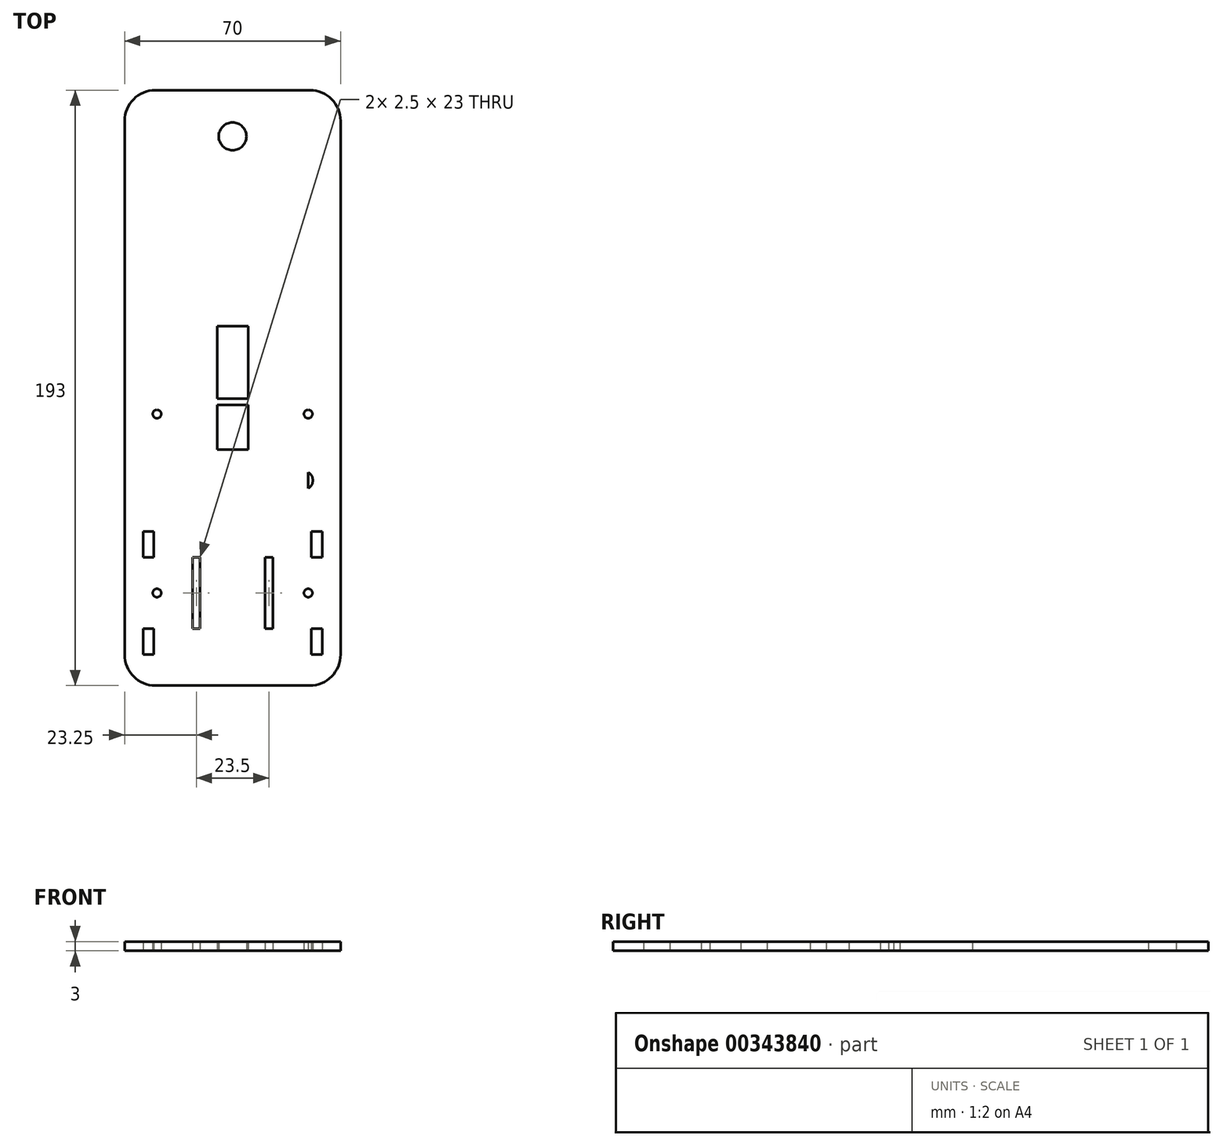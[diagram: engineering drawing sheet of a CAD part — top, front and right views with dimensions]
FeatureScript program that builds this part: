
annotation { "Feature Type Name" : "Feature", "Feature Type Description" : "" }
export const myFeature = defineFeature(function(context is Context, id is Id, definition is map)
    precondition{}
    {
        {
            var Q0;
            Q0=qCreatedBy(makeId("Top.planeOp"),FACE);
            var sketch = newSketch(context, id + "F0", { "sketchPlane" : qUnion([Q0])});
            skLineSegment(sketch, "E0.bottom", {"start": v(-25, 96.5) * mm, "end": v(25, 96.5) * mm});
            skLineSegment(sketch, "E0.top", {"start": v(-25, -96.5) * mm, "end": v(25, -96.5) * mm});
            skLineSegment(sketch, "E0.left", {"start": v(-35, 86.5) * mm, "end": v(-35, -86.5) * mm});
            skLineSegment(sketch, "E0.right", {"start": v(35, 86.5) * mm, "end": v(35, -86.5) * mm});
            skPoint(sketch, "E0.middle", {"position": v(0, 0) * mm});
            skLineSegment(sketch, "E1.bottom", {"start": v(-29, -78) * mm, "end": v(-25.5, -78) * mm});
            skLineSegment(sketch, "E1.top", {"start": v(-29, -86.5) * mm, "end": v(-25.5, -86.5) * mm});
            skLineSegment(sketch, "E1.left", {"start": v(-29, -78) * mm, "end": v(-29, -86.5) * mm});
            skLineSegment(sketch, "E1.right", {"start": v(-25.5, -78) * mm, "end": v(-25.5, -86.5) * mm});
            skLineSegment(sketch, "E2.bottom", {"start": v(-29, -55) * mm, "end": v(-25.5, -55) * mm});
            skLineSegment(sketch, "E2.top", {"start": v(-29, -46.5) * mm, "end": v(-25.5, -46.5) * mm});
            skLineSegment(sketch, "E2.left", {"start": v(-29, -55) * mm, "end": v(-29, -46.5) * mm});
            skLineSegment(sketch, "E2.right", {"start": v(-25.5, -55) * mm, "end": v(-25.5, -46.5) * mm});
            skLineSegment(sketch, "E3.MirrorCS", {"start": v(29, -55) * mm, "end": v(25.5, -55) * mm});
            skLineSegment(sketch, "E4.MirrorCS", {"start": v(29, -78) * mm, "end": v(25.5, -78) * mm});
            skLineSegment(sketch, "E5.MirrorCS", {"start": v(29, -86.5) * mm, "end": v(25.5, -86.5) * mm});
            skLineSegment(sketch, "E6.MirrorCS", {"start": v(29, -46.5) * mm, "end": v(25.5, -46.5) * mm});
            skLineSegment(sketch, "E7.MirrorCS", {"start": v(25.5, -55) * mm, "end": v(25.5, -46.5) * mm});
            skLineSegment(sketch, "E8.MirrorCS", {"start": v(29, -78) * mm, "end": v(29, -86.5) * mm});
            skLineSegment(sketch, "E9.MirrorCS", {"start": v(25.5, -78) * mm, "end": v(25.5, -86.5) * mm});
            skLineSegment(sketch, "E10.MirrorCS", {"start": v(29, -55) * mm, "end": v(29, -46.5) * mm});
            skCircle(sketch, "E11", {"center": v(0, 81.5) * mm, "radius": 4.5 * mm});
            skPoint(sketch, "E12.visualSharp", {"position": v(35, 96.5) * mm});
            skArc(sketch, "E12.filletArc", {"start": v(35, 86.5) * mm, "mid": v(32.07, 93.57) * mm, "end": v(25, 96.5) * mm});
            skPoint(sketch, "E13.visualSharp", {"position": v(-35, 96.5) * mm});
            skArc(sketch, "E13.filletArc", {"start": v(-25, 96.5) * mm, "mid": v(-32.07, 93.57) * mm, "end": v(-35, 86.5) * mm});
            skPoint(sketch, "E14.visualSharp", {"position": v(35, -96.5) * mm});
            skArc(sketch, "E14.filletArc", {"start": v(25, -96.5) * mm, "mid": v(32.07, -93.57) * mm, "end": v(35, -86.5) * mm});
            skPoint(sketch, "E15.visualSharp", {"position": v(-35, -96.5) * mm});
            skArc(sketch, "E15.filletArc", {"start": v(-35, -86.5) * mm, "mid": v(-32.07, -93.57) * mm, "end": v(-25, -96.5) * mm});
            skLineSegment(sketch, "E16.bottom", {"start": v(-5, 20) * mm, "end": v(5, 20) * mm});
            skLineSegment(sketch, "E16.top", {"start": v(-5, -20) * mm, "end": v(5, -20) * mm});
            skLineSegment(sketch, "E16.left", {"start": v(-5, 20) * mm, "end": v(-5, -20) * mm});
            skLineSegment(sketch, "E16.right", {"start": v(5, 20) * mm, "end": v(5, -20) * mm});
            skLineSegment(sketch, "E17.bottom", {"start": v(-13, -55) * mm, "end": v(-10.5, -55) * mm});
            skLineSegment(sketch, "E17.top", {"start": v(-13, -78) * mm, "end": v(-10.5, -78) * mm});
            skLineSegment(sketch, "E17.left", {"start": v(-13, -55) * mm, "end": v(-13, -78) * mm});
            skLineSegment(sketch, "E17.right", {"start": v(-10.5, -55) * mm, "end": v(-10.5, -78) * mm});
            skLineSegment(sketch, "E18.MirrorCS", {"start": v(13, -55) * mm, "end": v(10.5, -55) * mm});
            skLineSegment(sketch, "E19.MirrorCS", {"start": v(13, -78) * mm, "end": v(10.5, -78) * mm});
            skLineSegment(sketch, "E20.MirrorCS", {"start": v(10.5, -55) * mm, "end": v(10.5, -78) * mm});
            skLineSegment(sketch, "E21.MirrorCS", {"start": v(13, -55) * mm, "end": v(13, -78) * mm});
            skCircle(sketch, "E22", {"center": v(24.5, -8.5) * mm, "radius": 1.37 * mm});
            skCircle(sketch, "E23", {"center": v(24.5, -66.5) * mm, "radius": 1.38 * mm});
            skCircle(sketch, "E24", {"center": v(-24.5, -66.5) * mm, "radius": 1.38 * mm});
            skCircle(sketch, "E25", {"center": v(-24.5, -8.5) * mm, "radius": 1.38 * mm});
            skLineSegment(sketch, "E26", {"start": v(24.5, -8.5) * mm, "end": v(24.5, -66.5) * mm});
            skLineSegment(sketch, "E27", {"start": v(24.5, -66.5) * mm, "end": v(-24.5, -66.5) * mm});
            skPoint(sketch, "E28", {"position": v(0, -37.5) * mm});
            skPoint(sketch, "E28.positionSnap0", {"position": v(0, -66.5) * mm});
            skPoint(sketch, "E28.positionSnap1", {"position": v(24.5, -37.5) * mm});
            skLineSegment(sketch, "E29.bottom", {"start": v(-13, -55) * mm, "end": v(-18.5, -55) * mm});
            skLineSegment(sketch, "E29.top", {"start": v(-13, -78) * mm, "end": v(-18.5, -78) * mm});
            skLineSegment(sketch, "E29.right", {"start": v(-18.5, -55) * mm, "end": v(-18.5, -78) * mm});
            skLineSegment(sketch, "E30.bottom", {"start": v(-10.5, -78) * mm, "end": v(-25.5, -78) * mm});
            skLineSegment(sketch, "E30.top", {"start": v(-10.5, -86.5) * mm, "end": v(-25.5, -86.5) * mm});
            skLineSegment(sketch, "E30.left", {"start": v(-10.5, -78) * mm, "end": v(-10.5, -86.5) * mm});
            skLineSegment(sketch, "E31.MirrorCS", {"start": v(13, -55) * mm, "end": v(18.5, -55) * mm});
            skLineSegment(sketch, "E32.MirrorCS", {"start": v(18.5, -55) * mm, "end": v(18.5, -78) * mm});
            skLineSegment(sketch, "E33.MirrorCS", {"start": v(10.5, -78) * mm, "end": v(25.5, -78) * mm});
            skLineSegment(sketch, "E34.MirrorCS", {"start": v(10.5, -86.5) * mm, "end": v(25.5, -86.5) * mm});
            skLineSegment(sketch, "E35.MirrorCS", {"start": v(10.5, -78) * mm, "end": v(10.5, -86.5) * mm});
            skLineSegment(sketch, "E36.bottom", {"start": v(-13, -78) * mm, "end": v(-29, -78) * mm});
            skLineSegment(sketch, "E36.top", {"start": v(-13, -55) * mm, "end": v(-29, -55) * mm});
            skLineSegment(sketch, "E36.left", {"start": v(-13, -78) * mm, "end": v(-13, -55) * mm});
            skLineSegment(sketch, "E36.right", {"start": v(-29, -78) * mm, "end": v(-29, -55) * mm});
            skLineSegment(sketch, "E37.MirrorCS", {"start": v(29, -78) * mm, "end": v(29, -55) * mm});
            skLineSegment(sketch, "E38.MirrorCS", {"start": v(13, -55) * mm, "end": v(29, -55) * mm});
            skCircle(sketch, "E39", {"center": v(0, -30) * mm, "radius": 20 * mm});
            skCircle(sketch, "E40.0", {"center": v(0, -30) * mm, "radius": 22 * mm});
            skCircle(sketch, "E41", {"center": v(-23, -30) * mm, "radius": 1 * mm});
            skCircle(sketch, "E42.0", {"center": v(-23, -30) * mm, "radius": 3 * mm});
            skCircle(sketch, "E43.MirrorC", {"center": v(23, -30) * mm, "radius": 1 * mm});
            skCircle(sketch, "E44.MirrorC", {"center": v(23, -30) * mm, "radius": 3 * mm});
            skLineSegment(sketch, "E45", {"start": v(-10.5, -55) * mm, "end": v(10.5, -55) * mm, "construction": true});
            skLineSegment(sketch, "E46.bottom", {"start": v(30, -3.5) * mm, "end": v(-30, -3.5) * mm});
            skLineSegment(sketch, "E46.top", {"start": v(30, 51.5) * mm, "end": v(-30, 51.5) * mm});
            skLineSegment(sketch, "E46.left", {"start": v(30, -3.5) * mm, "end": v(30, 51.5) * mm});
            skLineSegment(sketch, "E46.right", {"start": v(-30, -3.5) * mm, "end": v(-30, 51.5) * mm});
            skPoint(sketch, "E46.middle", {"position": v(0, 24) * mm});
            skLineSegment(sketch, "E47.0", {"start": v(20, 6.5) * mm, "end": v(20, 41.5) * mm});
            skLineSegment(sketch, "E47.1", {"start": v(20, 6.5) * mm, "end": v(-20, 6.5) * mm});
            skLineSegment(sketch, "E47.2", {"start": v(-20, 6.5) * mm, "end": v(-20, 41.5) * mm});
            skLineSegment(sketch, "E47.3", {"start": v(20, 41.5) * mm, "end": v(-20, 41.5) * mm});
            skLineSegment(sketch, "E48.0", {"start": v(32, 53.5) * mm, "end": v(-30, 53.5) * mm});
            skLineSegment(sketch, "E48.1", {"start": v(32, -5.5) * mm, "end": v(32, 53.5) * mm});
            skLineSegment(sketch, "E48.2", {"start": v(32, -5.5) * mm, "end": v(-30, -5.5) * mm});
            skLineSegment(sketch, "E49", {"start": v(-30, 51.5) * mm, "end": v(-30, 53.5) * mm});
            skLineSegment(sketch, "E50", {"start": v(-30, -5.5) * mm, "end": v(-30, -3.5) * mm});
            skLineSegment(sketch, "E51", {"start": v(-20, 41.5) * mm, "end": v(-30, 41.5) * mm});
            skLineSegment(sketch, "E52", {"start": v(20, 41.5) * mm, "end": v(32, 41.5) * mm});
            skLineSegment(sketch, "E53", {"start": v(32, 41.5) * mm, "end": v(20, 41.5) * mm});
            skLineSegment(sketch, "E54", {"start": v(20, 53.5) * mm, "end": v(20, 41.5) * mm});
            skLineSegment(sketch, "E55", {"start": v(20, 6.5) * mm, "end": v(32, 6.5) * mm});
            skLineSegment(sketch, "E56", {"start": v(20, 6.5) * mm, "end": v(20, -5.5) * mm});
            skLineSegment(sketch, "E57", {"start": v(-20, 6.5) * mm, "end": v(-20, -5.5) * mm});
            skLineSegment(sketch, "E58", {"start": v(-20, 41.5) * mm, "end": v(-20, 53.5) * mm});
            skLineSegment(sketch, "E59", {"start": v(-20, 6.5) * mm, "end": v(-30, 6.5) * mm});
            skCircle(sketch, "E60", {"center": v(-17, -8.5) * mm, "radius": 1 * mm});
            skCircle(sketch, "E61.0", {"center": v(-17, -8.5) * mm, "radius": 3 * mm});
            skCircle(sketch, "E62", {"center": v(-27, 56.5) * mm, "radius": 1 * mm});
            skCircle(sketch, "E63.0", {"center": v(-27, 56.5) * mm, "radius": 3 * mm});
            skLineSegment(sketch, "E64", {"start": v(-30, 53.5) * mm, "end": v(-30, 56.5) * mm});
            skLineSegment(sketch, "E65", {"start": v(-24, 56.5) * mm, "end": v(-24, 53.5) * mm});
            skLineSegment(sketch, "E66", {"start": v(-14, -8.5) * mm, "end": v(-14, -5.5) * mm});
            skLineSegment(sketch, "E67", {"start": v(-20, -8.5) * mm, "end": v(-20, -5.5) * mm});
            skLineSegment(sketch, "E68.bottom", {"start": v(-30, 53.5) * mm, "end": v(-32, 53.5) * mm});
            skLineSegment(sketch, "E68.top", {"start": v(-30, -5.5) * mm, "end": v(-32, -5.5) * mm});
            skLineSegment(sketch, "E68.left", {"start": v(-30, 53.5) * mm, "end": v(-30, -5.5) * mm});
            skLineSegment(sketch, "E68.right", {"start": v(-32, 53.5) * mm, "end": v(-32, -5.5) * mm});
            skLineSegment(sketch, "E69", {"start": v(-30, 41.5) * mm, "end": v(-32, 41.5) * mm});
            skLineSegment(sketch, "E70", {"start": v(-30, 6.5) * mm, "end": v(-32, 6.5) * mm});
            skSolve(sketch);
        }
        {
            var Q0;
            Q0=makeQuery(id+"F0.imprint","IMPRINT",FACE,{"disambiguationData":[TD([[makeQuery(id+"F0.imprint","IMPRINT",EDGE,{"derivedFrom":sQuery(id+"F0.wireOp",EDGE,"E0.bottom")}),-1.0]])]});
            var Q1;
            {var subQ0=sQuery(id+"F0.wireOp",EDGE,"0ZoFnGFM-cKHT-HDos-aa4S-ERoNxdyYTCCv.left");Q1=makeQuery(id+"F0.imprint","IMPRINT",FACE,{"disambiguationData":[TD([[makeQuery(id+"F0.imprint","IMPRINT",EDGE,{"derivedFrom":subQ0}),1.0]])]});}
            var Q2;
            {var subQ0=sQuery(id+"F0.wireOp",EDGE,"0ZoFnGFM-cKHT-HDos-aa4S-ERoNxdyYTCCv.left");Q2=makeQuery(id+"F0.imprint","IMPRINT",FACE,{"disambiguationData":[TD([[makeQuery(id+"F0.imprint","IMPRINT",EDGE,{"derivedFrom":subQ0}),-1.0]])]});}
            var Q3;
            {var subQ0=sQuery(id+"F0.wireOp",EDGE,"E29.right");var subQ1=sQuery(id+"F0.wireOp",EDGE,"E27");var subQ2=makeQuery(id+"F0.imprint","INTERSECT",VERTEX,{"derivedFrom":[subQ1,subQ0]});Q3=makeQuery(id+"F0.imprint","IMPRINT",FACE,{"disambiguationData":[TD([[makeQuery(id+"F0.imprint","IMPRINT",EDGE,{"disambiguationData":[TD([[subQ2,1.0]])],"derivedFrom":subQ1}),1.0]])]});}
            var Q4;
            {var subQ5=sQuery(id+"F0.wireOp",EDGE,"E29.bottom");Q4=makeQuery(id+"F0.imprint","IMPRINT",FACE,{"disambiguationData":[TD([[makeQuery(id+"F0.imprint","IMPRINT",EDGE,{"derivedFrom":subQ5}),1.0]])]});}
            var Q5;
            Q5=makeQuery(id+"F0.imprint","IMPRINT",FACE,{"disambiguationData":[TD([[makeQuery(id+"F0.imprint","IMPRINT",EDGE,{"derivedFrom":sQuery(id+"F0.wireOp",EDGE,"E30.top")}),-1.0]])]});
            var Q6;
            {var subQ1=sQuery(id+"F0.wireOp",EDGE,"E9.MirrorCS");Q6=makeQuery(id+"F0.imprint","IMPRINT",FACE,{"disambiguationData":[TD([[makeQuery(id+"F0.imprint","IMPRINT",EDGE,{"derivedFrom":subQ1}),-1.0]])]});}
            var Q7;
            {var subQ0=sQuery(id+"F0.wireOp",EDGE,"E33.MirrorCS");var subQ1=sQuery(id+"F0.wireOp",EDGE,"E21.MirrorCS");var subQ2=makeQuery(id+"F0.imprint","INTERSECT",VERTEX,{"derivedFrom":[subQ1,subQ0]});Q7=makeQuery(id+"F0.imprint","IMPRINT",FACE,{"disambiguationData":[TD([[makeQuery(id+"F0.imprint","IMPRINT",EDGE,{"disambiguationData":[TD([[subQ2,1.0]])],"derivedFrom":subQ1}),1.0]])]});}
            var Q8;
            {var subQ0=sQuery(id+"F0.wireOp",EDGE,"E31.MirrorCS");Q8=makeQuery(id+"F0.imprint","IMPRINT",FACE,{"disambiguationData":[TD([[makeQuery(id+"F0.imprint","IMPRINT",EDGE,{"derivedFrom":subQ0}),-1.0]])]});}
            var Q9;
            Q9=makeQuery(id+"F0.imprint","IMPRINT",FACE,{"disambiguationData":[TD([[makeQuery(id+"F0.imprint","IMPRINT",EDGE,{"derivedFrom":sQuery(id+"F0.wireOp",EDGE,"E24")}),-1.0]])]});
            var Q10;
            {var subQ0=sQuery(id+"F0.wireOp",EDGE,"E29.right");var subQ1=sQuery(id+"F0.wireOp",EDGE,"E27");var subQ2=makeQuery(id+"F0.imprint","INTERSECT",VERTEX,{"derivedFrom":[subQ1,subQ0]});Q10=makeQuery(id+"F0.imprint","IMPRINT",FACE,{"disambiguationData":[TD([[makeQuery(id+"F0.imprint","IMPRINT",EDGE,{"disambiguationData":[TD([[subQ2,1.0]])],"derivedFrom":subQ1}),-1.0]])]});}
            var Q11;
            {var subQ5=sQuery(id+"F0.wireOp",EDGE,"E23");var subQ7=sQuery(id+"F0.wireOp",EDGE,"E26");var subQ9=makeQuery(id+"F0.imprint","INTERSECT",VERTEX,{"derivedFrom":[subQ5,subQ7]});Q11=makeQuery(id+"F0.imprint","IMPRINT",FACE,{"disambiguationData":[TD([[makeQuery(id+"F0.imprint","IMPRINT",EDGE,{"disambiguationData":[TD([[subQ9,-1.0]])],"derivedFrom":subQ5}),-1.0]])]});}
            var Q12;
            {var subQ1=sQuery(id+"F0.wireOp",EDGE,"E21.MirrorCS");var subQ3=sQuery(id+"F0.wireOp",EDGE,"E27");var subQ4=makeQuery(id+"F0.imprint","INTERSECT",VERTEX,{"derivedFrom":[subQ1,subQ3]});Q12=makeQuery(id+"F0.imprint","IMPRINT",FACE,{"disambiguationData":[TD([[makeQuery(id+"F0.imprint","IMPRINT",EDGE,{"disambiguationData":[TD([[subQ4,1.0]])],"derivedFrom":subQ3}),-1.0]])]});}
            var Q13;
            {var subQ11=sQuery(id+"F0.wireOp",EDGE,"E4.MirrorCS");Q13=makeQuery(id+"F0.imprint","IMPRINT",FACE,{"disambiguationData":[TD([[makeQuery(id+"F0.imprint","IMPRINT",EDGE,{"derivedFrom":subQ11}),-1.0]])]});}
            var Q14;
            {var subQ4=sQuery(id+"F0.wireOp",EDGE,"E16.top");Q14=makeQuery(id+"F0.imprint","IMPRINT",FACE,{"disambiguationData":[TD([[makeQuery(id+"F0.imprint","IMPRINT",EDGE,{"derivedFrom":subQ4}),-1.0]])]});}
            var Q15;
            {var subQ0=sQuery(id+"F0.wireOp",EDGE,"E40.0");var subQ1=sQuery(id+"F0.wireOp",EDGE,"E16.left");var subQ2=makeQuery(id+"F0.imprint","INTERSECT",VERTEX,{"derivedFrom":[subQ1,subQ0]});Q15=makeQuery(id+"F0.imprint","IMPRINT",FACE,{"disambiguationData":[TD([[makeQuery(id+"F0.imprint","IMPRINT",EDGE,{"disambiguationData":[TD([[subQ2,-1.0]])],"derivedFrom":subQ1}),-1.0]])]});}
            var Q16;
            {var subQ0=sQuery(id+"F0.wireOp",EDGE,"E40.0");var subQ1=makeQuery(id+"F0.imprint","INTERSECT",VERTEX,{"derivedFrom":[subQ0,sQuery(id+"F0.wireOp",EDGE,"E41")]});Q16=makeQuery(id+"F0.imprint","IMPRINT",FACE,{"disambiguationData":[TD([[makeQuery(id+"F0.imprint","IMPRINT",EDGE,{"disambiguationData":[TD([[subQ1,1.0]])],"derivedFrom":subQ0}),1.0]])]});}
            var Q17;
            {var subQ0=sQuery(id+"F0.wireOp",EDGE,"E44.MirrorC");var subQ1=sQuery(id+"F0.wireOp",EDGE,"E39");var subQ2=makeQuery(id+"F0.imprint","INTERSECT",VERTEX,{"derivedFrom":[subQ1,subQ0]});Q17=makeQuery(id+"F0.imprint","IMPRINT",FACE,{"disambiguationData":[TD([[makeQuery(id+"F0.imprint","IMPRINT",EDGE,{"disambiguationData":[TD([[subQ2,1.0]])],"derivedFrom":subQ1}),-1.0]])]});}
            var Q18;
            {var subQ0=sQuery(id+"F0.wireOp",EDGE,"E41");Q18=makeQuery(id+"F0.imprint","IMPRINT",FACE,{"disambiguationData":[TD([[makeQuery(id+"F0.imprint","IMPRINT",EDGE,{"derivedFrom":subQ0}),-1.0]])]});}
            var Q19;
            Q19=makeQuery(id+"F0.imprint","IMPRINT",FACE,{"disambiguationData":[TD([[makeQuery(id+"F0.imprint","IMPRINT",EDGE,{"derivedFrom":sQuery(id+"F0.wireOp",EDGE,"E41")}),1.0]])]});
            var Q20;
            {var subQ0=sQuery(id+"F0.wireOp",EDGE,"E40.0");var subQ1=makeQuery(id+"F0.imprint","INTERSECT",VERTEX,{"derivedFrom":[subQ0,sQuery(id+"F0.wireOp",EDGE,"E43.MirrorC")]});Q20=makeQuery(id+"F0.imprint","IMPRINT",FACE,{"disambiguationData":[TD([[makeQuery(id+"F0.imprint","IMPRINT",EDGE,{"disambiguationData":[TD([[subQ1,-1.0]])],"derivedFrom":subQ0}),1.0]])]});}
            var Q21;
            {var subQ0=sQuery(id+"F0.wireOp",EDGE,"E40.0");var subQ1=sQuery(id+"F0.wireOp",EDGE,"E16.right");var subQ2=makeQuery(id+"F0.imprint","INTERSECT",VERTEX,{"derivedFrom":[subQ1,subQ0]});Q21=makeQuery(id+"F0.imprint","IMPRINT",FACE,{"disambiguationData":[TD([[makeQuery(id+"F0.imprint","IMPRINT",EDGE,{"disambiguationData":[TD([[subQ2,-1.0]])],"derivedFrom":subQ1}),1.0]])]});}
            var Q22;
            {var subQ0=sQuery(id+"F0.wireOp",EDGE,"E43.MirrorC");Q22=makeQuery(id+"F0.imprint","IMPRINT",FACE,{"disambiguationData":[TD([[makeQuery(id+"F0.imprint","IMPRINT",EDGE,{"derivedFrom":subQ0}),1.0]])]});}
            var Q23;
            {var subQ0=sQuery(id+"F0.wireOp",EDGE,"E44.MirrorC");var subQ1=sQuery(id+"F0.wireOp",EDGE,"E26");var subQ2=makeQuery(id+"F0.imprint","INTERSECT",VERTEX,{"disambiguationData":[OD(0.0)],"derivedFrom":[subQ1,subQ0]});Q23=makeQuery(id+"F0.imprint","IMPRINT",FACE,{"disambiguationData":[TD([[makeQuery(id+"F0.imprint","IMPRINT",EDGE,{"disambiguationData":[TD([[subQ2,-1.0]])],"derivedFrom":subQ1}),1.0]])]});}
            var Q24;
            Q24=makeQuery(id+"F0.imprint","IMPRINT",FACE,{"disambiguationData":[TD([[makeQuery(id+"F0.imprint","IMPRINT",EDGE,{"derivedFrom":sQuery(id+"F0.wireOp",EDGE,"E43.MirrorC")}),-1.0]])]});
            var Q25;
            {var subQ2=sQuery(id+"F0.wireOp",EDGE,"E16.bottom");Q25=makeQuery(id+"F0.imprint","IMPRINT",FACE,{"disambiguationData":[TD([[makeQuery(id+"F0.imprint","IMPRINT",EDGE,{"derivedFrom":subQ2}),1.0]])]});}
            var Q26;
            Q26=makeQuery(id+"F0.imprint","IMPRINT",FACE,{"disambiguationData":[TD([[makeQuery(id+"F0.imprint","IMPRINT",EDGE,{"derivedFrom":sQuery(id+"F0.wireOp",EDGE,"E46.top")}),1.0]])]});
            var Q27;
            Q27=makeQuery(id+"F0.imprint","IMPRINT",FACE,{"disambiguationData":[TD([[makeQuery(id+"F0.imprint","IMPRINT",EDGE,{"derivedFrom":sQuery(id+"F0.wireOp",EDGE,"E46.top")}),-1.0]])]});
            var Q28;
            {var subQ5=sQuery(id+"F0.wireOp",EDGE,"E50");Q28=makeQuery(id+"F0.imprint","IMPRINT",FACE,{"disambiguationData":[TD([[makeQuery(id+"F0.imprint","IMPRINT",EDGE,{"derivedFrom":subQ5}),-1.0]])]});}
            var Q29;
            Q29=makeQuery(id+"F0.imprint","IMPRINT",FACE,{"disambiguationData":[TD([[makeQuery(id+"F0.imprint","IMPRINT",EDGE,{"derivedFrom":sQuery(id+"F0.wireOp",EDGE,"E47.2")}),1.0]])]});
            var Q30;
            {var subQ5=sQuery(id+"F0.wireOp",EDGE,"E59");Q30=makeQuery(id+"F0.imprint","IMPRINT",FACE,{"disambiguationData":[TD([[makeQuery(id+"F0.imprint","IMPRINT",EDGE,{"derivedFrom":subQ5}),1.0]])]});}
            var Q31;
            {var subQ0=sQuery(id+"F0.wireOp",EDGE,"E47.1");var subQ1=sQuery(id+"F0.wireOp",EDGE,"E16.left");var subQ2=makeQuery(id+"F0.imprint","INTERSECT",VERTEX,{"derivedFrom":[subQ1,subQ0]});Q31=makeQuery(id+"F0.imprint","IMPRINT",FACE,{"disambiguationData":[TD([[makeQuery(id+"F0.imprint","IMPRINT",EDGE,{"disambiguationData":[TD([[subQ2,-1.0]])],"derivedFrom":subQ1}),-1.0]])]});}
            var Q32;
            {var subQ0=sQuery(id+"F0.wireOp",EDGE,"E46.bottom");var subQ1=sQuery(id+"F0.wireOp",EDGE,"E16.left");var subQ2=makeQuery(id+"F0.imprint","INTERSECT",VERTEX,{"derivedFrom":[subQ1,subQ0]});Q32=makeQuery(id+"F0.imprint","IMPRINT",FACE,{"disambiguationData":[TD([[makeQuery(id+"F0.imprint","IMPRINT",EDGE,{"disambiguationData":[TD([[subQ2,-1.0]])],"derivedFrom":subQ1}),-1.0]])]});}
            var Q33;
            {var subQ0=sQuery(id+"F0.wireOp",EDGE,"E47.1");var subQ1=sQuery(id+"F0.wireOp",EDGE,"E16.right");var subQ2=makeQuery(id+"F0.imprint","INTERSECT",VERTEX,{"derivedFrom":[subQ1,subQ0]});Q33=makeQuery(id+"F0.imprint","IMPRINT",FACE,{"disambiguationData":[TD([[makeQuery(id+"F0.imprint","IMPRINT",EDGE,{"disambiguationData":[TD([[subQ2,-1.0]])],"derivedFrom":subQ1}),1.0]])]});}
            var Q34;
            {var subQ0=sQuery(id+"F0.wireOp",EDGE,"E46.bottom");var subQ1=sQuery(id+"F0.wireOp",EDGE,"E16.right");var subQ2=makeQuery(id+"F0.imprint","INTERSECT",VERTEX,{"derivedFrom":[subQ1,subQ0]});Q34=makeQuery(id+"F0.imprint","IMPRINT",FACE,{"disambiguationData":[TD([[makeQuery(id+"F0.imprint","IMPRINT",EDGE,{"disambiguationData":[TD([[subQ2,-1.0]])],"derivedFrom":subQ1}),1.0]])]});}
            var Q35;
            {var subQ0=sQuery(id+"F0.wireOp",EDGE,"E46.left");var subQ1=sQuery(id+"F0.wireOp",EDGE,"E46.bottom");var subQ2=makeQuery(id+"F0.imprint","INTERSECT",VERTEX,{"derivedFrom":[subQ1,subQ0]});Q35=makeQuery(id+"F0.imprint","IMPRINT",FACE,{"disambiguationData":[TD([[makeQuery(id+"F0.imprint","IMPRINT",EDGE,{"disambiguationData":[TD([[subQ2,-1.0]])],"derivedFrom":subQ1}),-1.0]])]});}
            var Q36;
            {var subQ0=sQuery(id+"F0.wireOp",EDGE,"E55");var subQ1=sQuery(id+"F0.wireOp",EDGE,"E46.left");var subQ2=makeQuery(id+"F0.imprint","INTERSECT",VERTEX,{"derivedFrom":[subQ1,subQ0]});Q36=makeQuery(id+"F0.imprint","IMPRINT",FACE,{"disambiguationData":[TD([[makeQuery(id+"F0.imprint","IMPRINT",EDGE,{"disambiguationData":[TD([[subQ2,-1.0]])],"derivedFrom":subQ1}),-1.0]])]});}
            var Q37;
            {var subQ7=sQuery(id+"F0.wireOp",EDGE,"E46.left");var subQ8=sQuery(id+"F0.wireOp",EDGE,"E46.bottom");var subQ9=makeQuery(id+"F0.imprint","INTERSECT",VERTEX,{"derivedFrom":[subQ8,subQ7]});Q37=makeQuery(id+"F0.imprint","IMPRINT",FACE,{"disambiguationData":[TD([[makeQuery(id+"F0.imprint","IMPRINT",EDGE,{"disambiguationData":[TD([[subQ9,-1.0]])],"derivedFrom":subQ8}),1.0]])]});}
            var Q38;
            {var subQ7=sQuery(id+"F0.wireOp",EDGE,"E46.top");var subQ9=sQuery(id+"F0.wireOp",EDGE,"E46.left");var subQ10=makeQuery(id+"F0.imprint","INTERSECT",VERTEX,{"derivedFrom":[subQ7,subQ9]});Q38=makeQuery(id+"F0.imprint","IMPRINT",FACE,{"disambiguationData":[TD([[makeQuery(id+"F0.imprint","IMPRINT",EDGE,{"disambiguationData":[TD([[subQ10,-1.0]])],"derivedFrom":subQ7}),-1.0]])]});}
            var Q39;
            {var subQ5=sQuery(id+"F0.wireOp",EDGE,"E47.0");Q39=makeQuery(id+"F0.imprint","IMPRINT",FACE,{"disambiguationData":[TD([[makeQuery(id+"F0.imprint","IMPRINT",EDGE,{"derivedFrom":subQ5}),-1.0]])]});}
            var Q40;
            {var subQ0=sQuery(id+"F0.wireOp",EDGE,"E49");Q40=makeQuery(id+"F0.imprint","IMPRINT",FACE,{"disambiguationData":[TD([[makeQuery(id+"F0.imprint","IMPRINT",EDGE,{"derivedFrom":subQ0}),-1.0]])]});}
            var Q41;
            {var subQ0=sQuery(id+"F0.wireOp",EDGE,"E65");var subQ1=sQuery(id+"F0.wireOp",EDGE,"E48.0");var subQ2=makeQuery(id+"F0.imprint","INTERSECT",VERTEX,{"derivedFrom":[subQ1,subQ0]});Q41=makeQuery(id+"F0.imprint","IMPRINT",FACE,{"disambiguationData":[TD([[makeQuery(id+"F0.imprint","IMPRINT",EDGE,{"disambiguationData":[TD([[subQ2,-1.0]])],"derivedFrom":subQ1}),-1.0]])]});}
            var Q42;
            {var subQ0=sQuery(id+"F0.wireOp",EDGE,"E64");Q42=makeQuery(id+"F0.imprint","IMPRINT",FACE,{"disambiguationData":[TD([[makeQuery(id+"F0.imprint","IMPRINT",EDGE,{"derivedFrom":subQ0}),-1.0]])]});}
            var Q43;
            Q43=makeQuery(id+"F0.imprint","IMPRINT",FACE,{"disambiguationData":[TD([[makeQuery(id+"F0.imprint","IMPRINT",EDGE,{"derivedFrom":sQuery(id+"F0.wireOp",EDGE,"E62")}),-1.0]])]});
            var Q44;
            Q44=makeQuery(id+"F0.imprint","IMPRINT",FACE,{"disambiguationData":[TD([[makeQuery(id+"F0.imprint","IMPRINT",EDGE,{"derivedFrom":sQuery(id+"F0.wireOp",EDGE,"E62")}),1.0]])]});
            var Q45;
            Q45=makeQuery(id+"F0.imprint","IMPRINT",FACE,{"disambiguationData":[TD([[makeQuery(id+"F0.imprint","IMPRINT",EDGE,{"derivedFrom":sQuery(id+"F0.wireOp",EDGE,"E60")}),1.0]])]});
            var Q46;
            Q46=makeQuery(id+"F0.imprint","IMPRINT",FACE,{"disambiguationData":[TD([[makeQuery(id+"F0.imprint","IMPRINT",EDGE,{"derivedFrom":sQuery(id+"F0.wireOp",EDGE,"E60")}),-1.0]])]});
            var Q47;
            {var subQ0=sQuery(id+"F0.wireOp",EDGE,"E67");Q47=makeQuery(id+"F0.imprint","IMPRINT",FACE,{"disambiguationData":[TD([[makeQuery(id+"F0.imprint","IMPRINT",EDGE,{"derivedFrom":subQ0}),-1.0]])]});}
            var Q48;
            {var subQ0=sQuery(id+"F0.wireOp",EDGE,"E66");Q48=makeQuery(id+"F0.imprint","IMPRINT",FACE,{"disambiguationData":[TD([[makeQuery(id+"F0.imprint","IMPRINT",EDGE,{"derivedFrom":subQ0}),1.0]])]});}
            var Q49;
            {var subQ0=sQuery(id+"F0.wireOp",EDGE,"E69");Q49=makeQuery(id+"F0.imprint","IMPRINT",FACE,{"disambiguationData":[TD([[makeQuery(id+"F0.imprint","IMPRINT",EDGE,{"derivedFrom":subQ0}),1.0]])]});}
            var Q50;
            {var subQ0=sQuery(id+"F0.wireOp",EDGE,"E68.left");var subQ1=sQuery(id+"F0.wireOp",EDGE,"E46.bottom");var subQ2=makeQuery(id+"F0.imprint","INTERSECT",VERTEX,{"derivedFrom":[subQ1,subQ0]});Q50=makeQuery(id+"F0.imprint","IMPRINT",FACE,{"disambiguationData":[TD([[makeQuery(id+"F0.imprint","IMPRINT",EDGE,{"disambiguationData":[TD([[subQ2,1.0]])],"derivedFrom":subQ1}),1.0]])]});}
            var Q51;
            {var subQ4=sQuery(id+"F0.wireOp",EDGE,"E68.bottom");Q51=makeQuery(id+"F0.imprint","IMPRINT",FACE,{"disambiguationData":[TD([[makeQuery(id+"F0.imprint","IMPRINT",EDGE,{"derivedFrom":subQ4}),1.0]])]});}
            var Q52;
            {var subQ0=sQuery(id+"F0.wireOp",EDGE,"E68.left");var subQ7=sQuery(id+"F0.wireOp",EDGE,"E46.top");var subQ8=makeQuery(id+"F0.imprint","INTERSECT",VERTEX,{"derivedFrom":[subQ7,subQ0]});Q52=makeQuery(id+"F0.imprint","IMPRINT",FACE,{"disambiguationData":[TD([[makeQuery(id+"F0.imprint","IMPRINT",EDGE,{"disambiguationData":[TD([[subQ8,1.0]])],"derivedFrom":subQ7}),-1.0]])]});}
            var Q53;
            {var subQ1=sQuery(id+"F0.wireOp",EDGE,"E68.top");Q53=makeQuery(id+"F0.imprint","IMPRINT",FACE,{"disambiguationData":[TD([[makeQuery(id+"F0.imprint","IMPRINT",EDGE,{"derivedFrom":subQ1}),-1.0]])]});}
            extrude(context, id + "F1", {"entities" : qUnion([Q0, Q1, Q2, Q3, Q4, Q5, Q6, Q7, Q8, Q9, Q10, Q11, Q12, Q13, Q14, Q15, Q16, Q17, Q18, Q19, Q20, Q21, Q22, Q23, Q24, Q25, Q26, Q27, Q28, Q29, Q30, Q31, Q32, Q33, Q34, Q35, Q36, Q37, Q38, Q39, Q40, Q41, Q42, Q43, Q44, Q45, Q46, Q47, Q48, Q49, Q50, Q51, Q52, Q53]), "depth" : 3 * mm, "offsetDistance" : 25 * mm});
        }
    });
